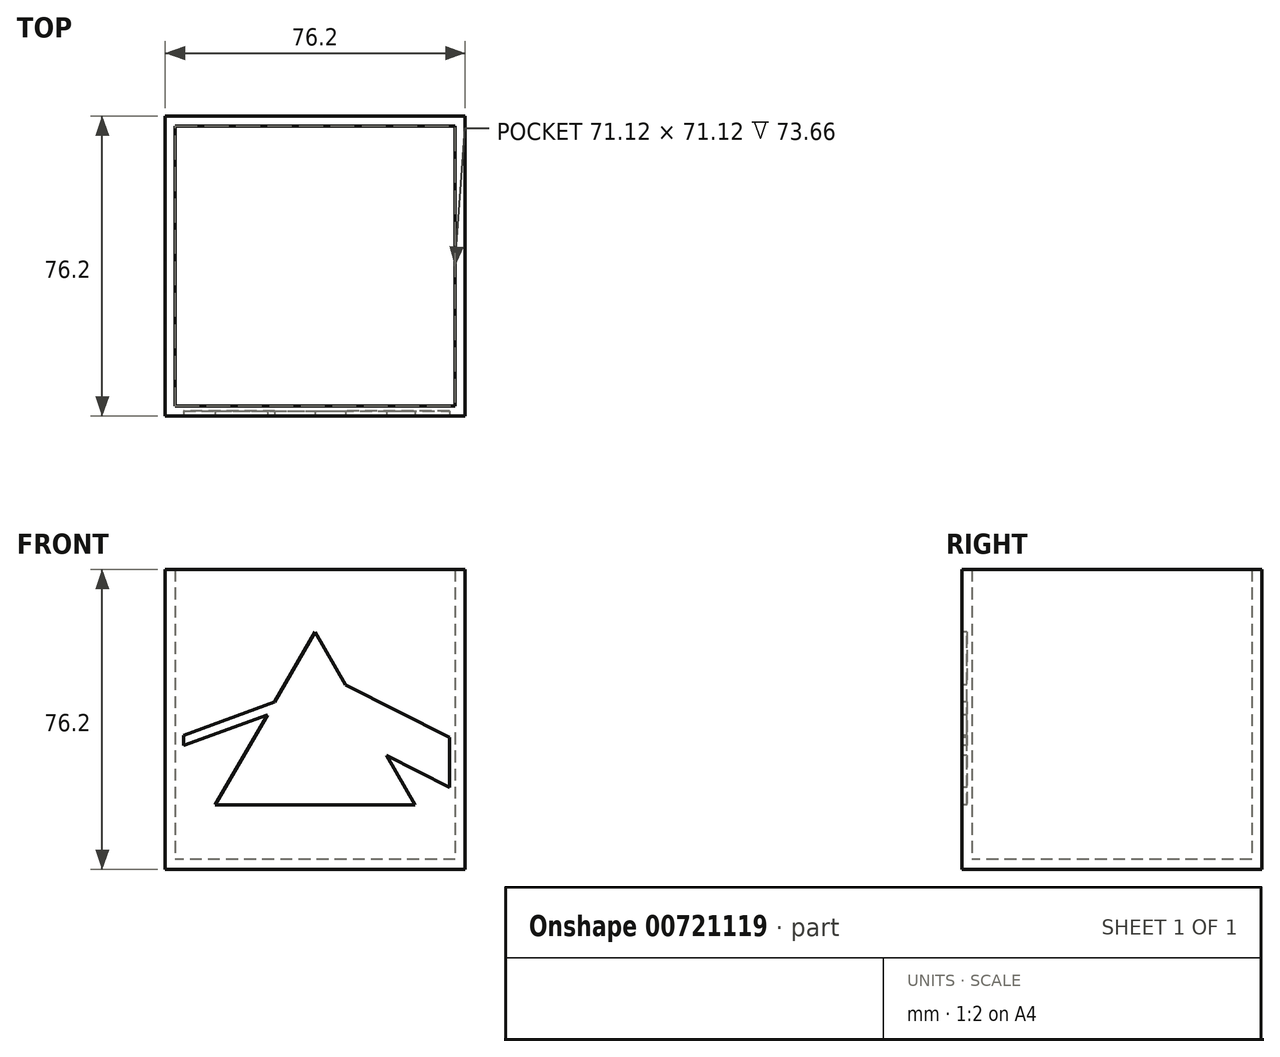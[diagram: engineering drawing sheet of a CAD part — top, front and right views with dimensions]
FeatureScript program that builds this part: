
annotation { "Feature Type Name" : "Feature", "Feature Type Description" : "" }
export const myFeature = defineFeature(function(context is Context, id is Id, definition is map)
    precondition{}
    {
        {
            var Q0;
            Q0=qCreatedBy(makeId("Top.planeOp"),FACE);
            var sketch = newSketch(context, id + "F0", { "sketchPlane" : qUnion([Q0])});
            skLineSegment(sketch, "E0.bottom", {"start": v(38.1, 38.1) * mm, "end": v(-38.1, 38.1) * mm});
            skLineSegment(sketch, "E0.top", {"start": v(38.1, -38.1) * mm, "end": v(-38.1, -38.1) * mm});
            skLineSegment(sketch, "E0.left", {"start": v(38.1, 38.1) * mm, "end": v(38.1, -38.1) * mm});
            skLineSegment(sketch, "E0.right", {"start": v(-38.1, 38.1) * mm, "end": v(-38.1, -38.1) * mm});
            skPoint(sketch, "E0.middle", {"position": v(0, 0) * mm});
            skSolve(sketch);
        }
        {
            var Q0;
            Q0 = qSketchRegion(id + "F0", true);
            extrude(context, id + "F1", {"entities" : qUnion([Q0]), "depth" : 2.54 * mm, "offsetDistance" : 25.4 * mm});
        }
        {
            var Q0;
            Q0=makeQuery(id+"F1.opExtrude","CAP_FACE",FACE,{"disambiguationData":[OSD([sQuery(id+"F0.wireOp",EDGE,"E0.bottom"),sQuery(id+"F0.wireOp",EDGE,"E0.top"),sQuery(id+"F0.wireOp",EDGE,"E0.left"),sQuery(id+"F0.wireOp",EDGE,"E0.right")])],"isStart":false});
            var sketch = newSketch(context, id + "F2", { "sketchPlane" : qUnion([Q0])});
            skLineSegment(sketch, "E1.bottom", {"start": v(35.56, 35.56) * mm, "end": v(-35.56, 35.56) * mm});
            skLineSegment(sketch, "E1.top", {"start": v(35.56, -35.56) * mm, "end": v(-35.56, -35.56) * mm});
            skLineSegment(sketch, "E1.left", {"start": v(35.56, 35.56) * mm, "end": v(35.56, -35.56) * mm});
            skLineSegment(sketch, "E1.right", {"start": v(-35.56, 35.56) * mm, "end": v(-35.56, -35.56) * mm});
            skPoint(sketch, "E1.middle", {"position": v(0, 0) * mm});
            skSolve(sketch);
        }
        {
            var Q0;
            Q0=makeQuery(id+"F2.imprint","IMPRINT",FACE,{"disambiguationData":[TD([[makeQuery(id+"F2.imprint","IMPRINT",EDGE,{"derivedFrom":sQuery(id+"F2.wireOp",EDGE,"E1.bottom")}),-1.0]])]});
            extrude(context, id + "F3", {"entities" : qUnion([Q0]), "operationType" : NewBodyOperationType.ADD, "depth" : 73.66 * mm, "offsetDistance" : 25.4 * mm});
        }
        {
            var Q0;
            {var subQ0=sQuery(id+"F0.wireOp",EDGE,"E0.top");Q0=makeQuery(id+"F3.boolean.opBoolean","MERGE",FACE,{"derivedFrom":[makeQuery(id+"F1.opExtrude","SWEPT_FACE",FACE,{"disambiguationData":[OSD([subQ0])]}),makeQuery(id+"F3.opExtrude","SWEPT_FACE",FACE,{"disambiguationData":[OSD([subQ0])]})]});}
            var sketch = newSketch(context, id + "F4", { "sketchPlane" : qUnion([Q0])});
            skLineSegment(sketch, "E2", {"start": v(-25.4, 16.33) * mm, "end": v(25.4, 16.33) * mm});
            skLineSegment(sketch, "E3", {"start": v(-25.4, 16.33) * mm, "end": v(0, 60.33) * mm});
            skLineSegment(sketch, "E4", {"start": v(0, 60.33) * mm, "end": v(25.4, 16.33) * mm});
            skLineSegment(sketch, "E5", {"start": v(-5.15, 44.38) * mm, "end": v(-33.41, 34.06) * mm});
            skLineSegment(sketch, "E6", {"start": v(-33.41, 34.06) * mm, "end": v(-33.41, 31.52) * mm});
            skLineSegment(sketch, "E7", {"start": v(-33.41, 31.52) * mm, "end": v(-5.15, 41.84) * mm});
            skLineSegment(sketch, "E8", {"start": v(-5.15, 41.84) * mm, "end": v(-5.15, 44.38) * mm});
            skLineSegment(sketch, "E9", {"start": v(3.81, 48.88) * mm, "end": v(3.81, 36.18) * mm});
            skLineSegment(sketch, "E10", {"start": v(3.81, 36.18) * mm, "end": v(34.13, 20.86) * mm});
            skLineSegment(sketch, "E11", {"start": v(34.13, 20.86) * mm, "end": v(34.13, 33.56) * mm});
            skLineSegment(sketch, "E12", {"start": v(34.13, 33.56) * mm, "end": v(3.81, 48.88) * mm});
            skSolve(sketch);
        }
        {
            var Q0;
            Q0=makeQuery(id+"F4.imprint","IMPRINT",FACE,{"disambiguationData":[TD([[makeQuery(id+"F4.imprint","IMPRINT",EDGE,{"derivedFrom":sQuery(id+"F4.wireOp",EDGE,"E2")}),1.0]])]});
            var Q1;
            {var subQ5=sQuery(id+"F4.wireOp",EDGE,"E6");Q1=makeQuery(id+"F4.imprint","IMPRINT",FACE,{"disambiguationData":[TD([[makeQuery(id+"F4.imprint","IMPRINT",EDGE,{"derivedFrom":subQ5}),1.0]])]});}
            var Q2;
            {var subQ5=sQuery(id+"F4.wireOp",EDGE,"E8");Q2=makeQuery(id+"F4.imprint","IMPRINT",FACE,{"disambiguationData":[TD([[makeQuery(id+"F4.imprint","IMPRINT",EDGE,{"derivedFrom":subQ5}),1.0]])]});}
            var Q3;
            {var subQ5=sQuery(id+"F4.wireOp",EDGE,"E9");Q3=makeQuery(id+"F4.imprint","IMPRINT",FACE,{"disambiguationData":[TD([[makeQuery(id+"F4.imprint","IMPRINT",EDGE,{"derivedFrom":subQ5}),1.0]])]});}
            var Q4;
            {var subQ5=sQuery(id+"F4.wireOp",EDGE,"E11");Q4=makeQuery(id+"F4.imprint","IMPRINT",FACE,{"disambiguationData":[TD([[makeQuery(id+"F4.imprint","IMPRINT",EDGE,{"derivedFrom":subQ5}),1.0]])]});}
            extrude(context, id + "F5", {"entities" : qUnion([Q0, Q1, Q2, Q3, Q4]), "operationType" : NewBodyOperationType.REMOVE, "oppositeDirection" : true, "depth" : 1.27 * mm, "offsetDistance" : 25.4 * mm});
        }
    });
